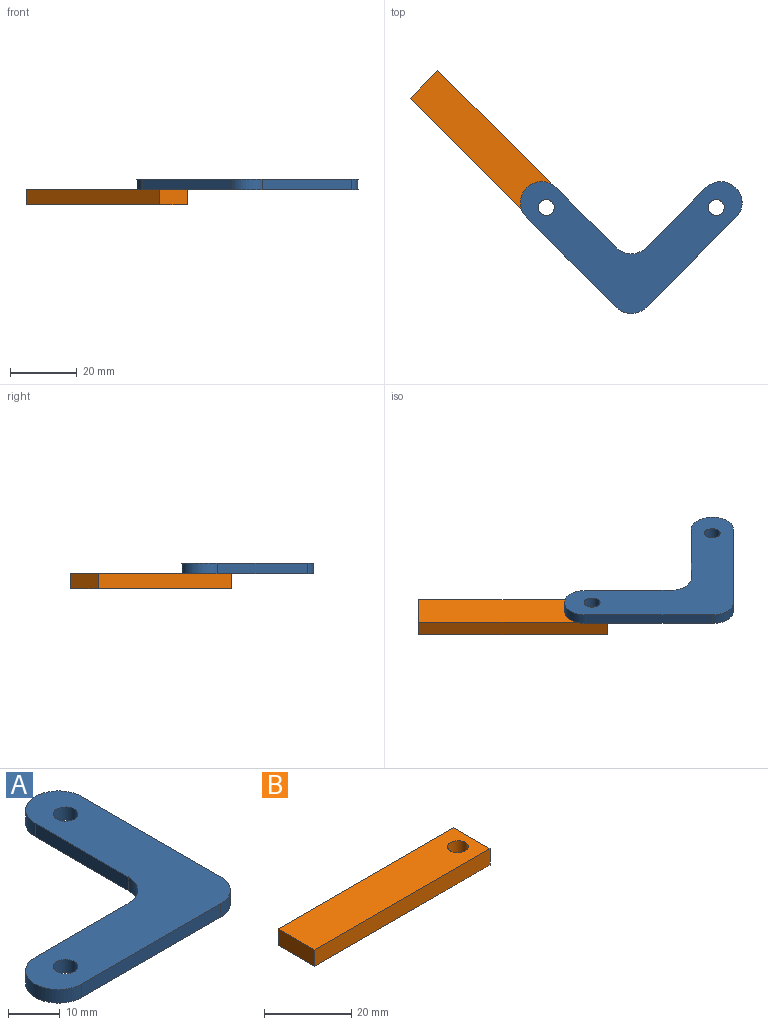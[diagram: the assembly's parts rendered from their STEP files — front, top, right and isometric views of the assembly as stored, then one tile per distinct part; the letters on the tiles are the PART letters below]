
ASSEMBLY  parts=2 mates=1
PART A: 12 faces, bbox 50.8x50.8x3.2 mm
  f0: plane 25.4x3.18mm, normal (0,1,0), area 80.6mm2, adj f6,f7,f8,f11
  f1: plane 38.1x3.18mm, normal (0,-1,0), area 121mm2, adj f6,f7,f8,f9
  f2: plane 38.1x3.18mm, normal (1,0,0), area 121mm2, adj f6,f7,f9,f10
  f3: cylinder r=2.38mm len=4.76mm, axis (0,0,-1), area 47.5mm2, adj f6,f7
  f4: cylinder r=2.38mm len=4.76mm, axis (0,0,-1), area 47.5mm2, adj f6,f7
  f5: plane 25.4x3.18mm, normal (-1,0,0), area 80.6mm2, adj f6,f7,f10,f11
  f6: plane 50.8x50.8mm, normal (0,0,1), area 1058.8mm2, adj f0,f1,f2,f3,f4,f5,f8,f9
  f7: plane 50.8x50.8mm, normal (0,0,-1), area 1058.8mm2, adj f0,f1,f2,f3,f4,f5,f8,f9
  f8: cylinder r=6.35mm len=12.7mm, axis (0,0,-1), area 63.3mm2, adj f0,f1,f6,f7
  f9: cylinder r=6.35mm len=6.35mm, axis (0,0,-1), area 31.7mm2, adj f1,f2,f6,f7
  f10: cylinder r=6.35mm len=12.7mm, axis (0,0,-1), area 63.3mm2, adj f2,f5,f6,f7
  f11: cylinder r=6.35mm len=6.35mm, axis (0,0,1), area 31.7mm2, adj f0,f5,f6,f7
PART B: 7 faces, bbox 56.8x11.8x4.6 mm
  f0: plane 56.79x4.57mm, normal (0,1,0), area 259.7mm2, adj f1,f4,f5,f6
  f1: plane 11.83x4.57mm, normal (-1,0,0), area 54.1mm2, adj f0,f2,f5,f6
  f2: plane 56.79x4.57mm, normal (0,-1,0), area 259.7mm2, adj f1,f4,f5,f6
  f3: cylinder r=2.38mm len=4.75mm, axis (0,0,-1), area 68.3mm2, adj f5,f6
  f4: plane 11.83x4.57mm, normal (1,0,0), area 54.1mm2, adj f0,f2,f5,f6
  f5: plane 56.79x11.83mm, normal (0,0,1), area 654mm2, adj f0,f1,f2,f3,f4
  f6: plane 56.79x11.83mm, normal (0,0,-1), area 654mm2, adj f0,f1,f2,f3,f4
PLACE A rot(axis=(0,0,-1),45deg) t=(6.91,-71.96,-12.45)mm
PLACE B rot(axis=(0,0,-1),45deg) t=(-23.67,-40.55,-17.02)mm
MATE fastened A.f3 <-> B.f3  axis (0,0,-1) through (17.29,-73.35,-12.45)mm
